# Revit family: Steelcase Turnstone - Campfire - Big Table
name_source: partatom
category: Furniture
revit_build: Autodesk Revit 2016 (Build: 20150714_1515(x64)
units: mm (PartAtom-declared; Revit-internal decimal feet)

## family parameters
Always vertical = Yes
Cut with Voids When Loaded = No
Room Calculation Point = No
Shared = No
Work Plane-Based = No

## types (10) — shared parameters
Assembly Code = E2020200
Manufacturer = Steelcase
Product = Campfire
Product Line = Turnstone
Release Date = April 2018
URL = https://www.steelcase.com
Width = 96.00"

## per-type parameters (varying)
| type | AutoCAD Tag | Center Panel Dist | Center Panel Height | Center Rail | Depth | Height | Power Cutout | Style Number(s) | Trough Void | With Trough | Without Through 24'' D | Without Trough 48'' D |
| 48D x 40H - Power Cutout | 48/96 | 23.69" | 38.29" | No | 48.00" | 40.27" | Yes | TS4TLP40 | 45.00" | No | No | Yes |
| 48D x 28H - Power Cutout | 48/96 | 23.69" | 26.29" | No | 48.00" | 28.00" | Yes | TS4TLP28 | 45.00" | No | No | Yes |
| 24D x 40H | 24/96 | 0.00" | 38.55" | No | 24.00" | 40.27" | No | TS4TLH40 | 45.00" | No | Yes | No |
| 24D x 28H | 24/96 | 0.00" | 26.29" | No | 24.00" | 28.00" | No | TS4TLH28 | 45.00" | No | Yes | No |
| 48D x 28H - Through/Center Rail | 48/96 | 23.69" | 26.29" | Yes | 48.00" | 28.00" | Yes | TS4TLT28 | 23.95" | Yes | No | No |
| 48D x 40H - Through/Center Rail | 48/96 | 23.69" | 38.29" | Yes | 48.39" | 40.00" | Yes | TS4TLT40 | 35.95" | Yes | No | No |
| 48D x 28H | 48/96 | 23.69" | 26.29" | No | 48.00" | 28.00" | No | TS4TL28 | 45.00" | No | No | Yes |
| 48D x 28H - Through | 48/96 | 23.69" | 26.29" | No | 48.00" | 28.00" | Yes | TS4TLT28 | 23.95" | Yes | No | No |
| 48D x 40H - Through | 48/96 | 23.69" | 38.29" | No | 48.39" | 40.00" | Yes | TS4TLT40 | 35.95" | Yes | No | No |
| 48D x 40H | 48/96 | 23.69" | 38.56" | No | 48.00" | 40.27" | No | TS4TL40 | 45.00" | No | No | Yes |

## geometry (parser evidence)
native form markers: Sweep x3
no freeform markers — native parametric forms only
